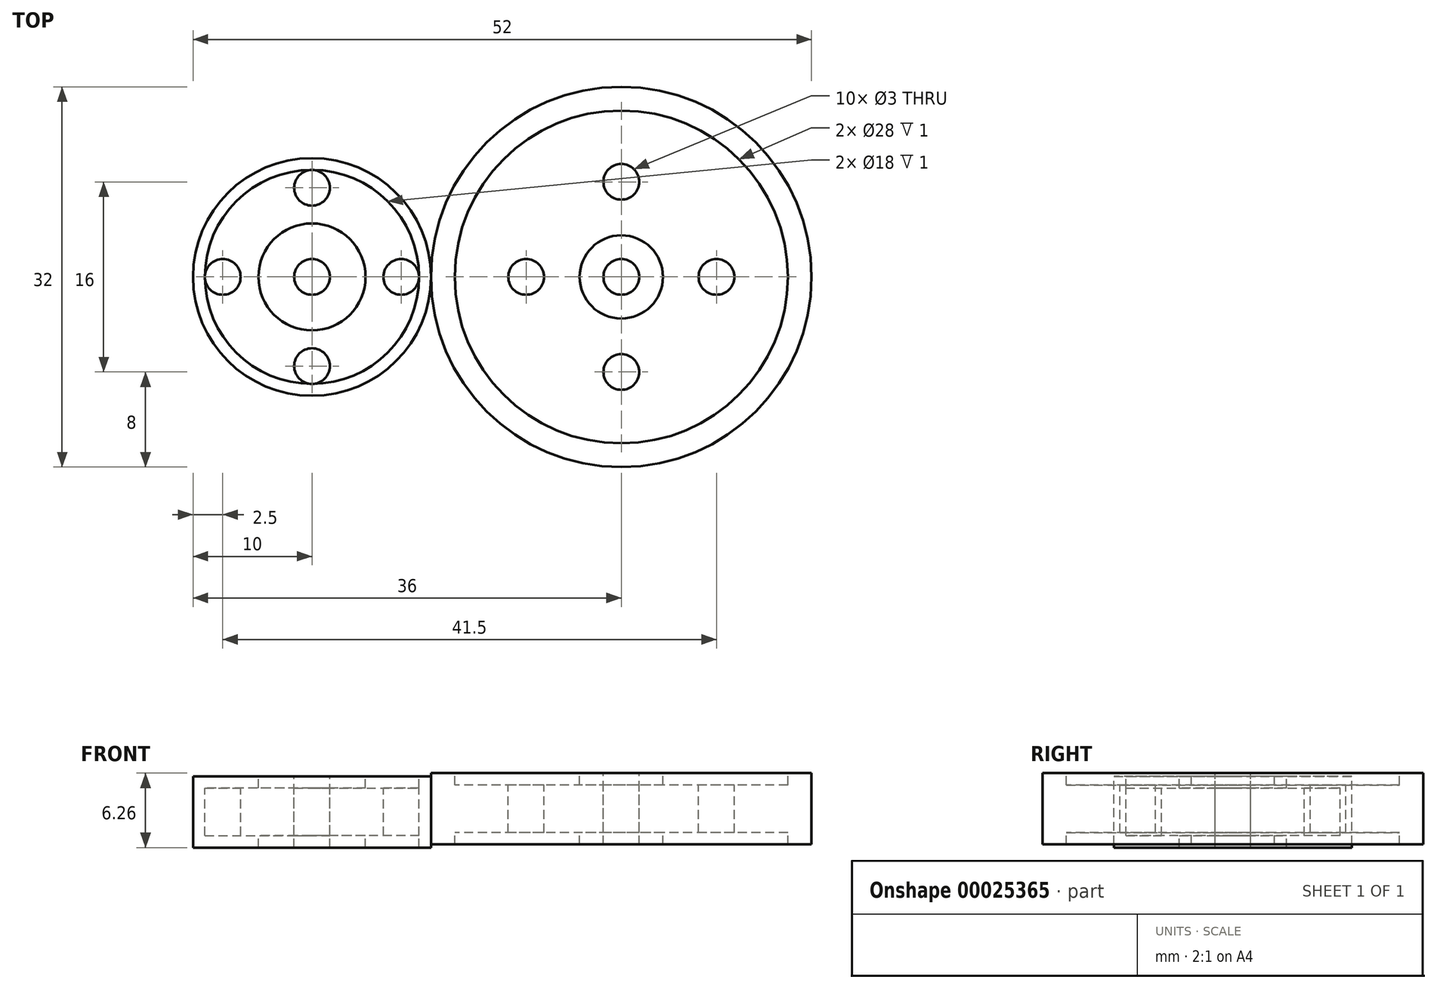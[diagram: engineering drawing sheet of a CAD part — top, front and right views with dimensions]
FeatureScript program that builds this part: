
annotation { "Feature Type Name" : "Feature", "Feature Type Description" : "" }
export const myFeature = defineFeature(function(context is Context, id is Id, definition is map)
    precondition{}
    {
        {
            var Q0;
            Q0=qCreatedBy(makeId("Front.planeOp"),FACE);
            var sketch = newSketch(context, id + "F0", { "sketchPlane" : qUnion([Q0])});
            skLineSegment(sketch, "E0", {"start": v(0, 6.2) * mm, "end": v(0, -6.7) * mm, "construction": true});
            skLineSegment(sketch, "E1.bottom", {"start": v(-4.5, 3.42) * mm, "end": v(-1.5, 3.42) * mm});
            skLineSegment(sketch, "E1.top", {"start": v(-4.5, -2.58) * mm, "end": v(-1.5, -2.58) * mm});
            skLineSegment(sketch, "E1.left", {"start": v(-4.5, 3.42) * mm, "end": v(-4.5, 2.42) * mm});
            skLineSegment(sketch, "E1.right", {"start": v(-1.5, 3.42) * mm, "end": v(-1.5, -2.58) * mm});
            skLineSegment(sketch, "E2.bottom", {"start": v(-4.5, 2.42) * mm, "end": v(-9, 2.42) * mm});
            skLineSegment(sketch, "E2.top", {"start": v(-4.5, -1.58) * mm, "end": v(-9, -1.58) * mm});
            skLineSegment(sketch, "E3.bottom", {"start": v(-9, 3.42) * mm, "end": v(-10, 3.42) * mm});
            skLineSegment(sketch, "E3.top", {"start": v(-9, -2.58) * mm, "end": v(-10, -2.58) * mm});
            skLineSegment(sketch, "E3.left", {"start": v(-9, 3.42) * mm, "end": v(-9, 2.42) * mm});
            skLineSegment(sketch, "E3.right", {"start": v(-10, 3.42) * mm, "end": v(-10, -2.58) * mm});
            skLineSegment(sketch, "E4.trimOffspring", {"start": v(-9, -1.58) * mm, "end": v(-9, -2.58) * mm});
            skLineSegment(sketch, "E5.trimOffspring", {"start": v(-4.5, -1.58) * mm, "end": v(-4.5, -2.58) * mm});
            skLineSegment(sketch, "E6", {"start": v(0, 6.2) * mm, "end": v(10, 6.2) * mm});
            skLineSegment(sketch, "E7", {"start": v(10, 6.2) * mm, "end": v(10, -16.38) * mm});
            skSolve(sketch);
        }
        {
            var Q0;
            Q0 = qSketchRegion(id + "F0", true);
            var Q1;
            Q1=sQuery(id+"F0.wireOp",EDGE,"E0");
            revolve(context, id + "F1", {"entities" : qUnion([Q0]), "axis" : qUnion([Q1]), "revolveType" : RevolveType.FULL});
        }
        {
            var Q0;
            Q0=makeQuery(id+"F1.opRevolve","SWEPT_FACE",FACE,{"disambiguationData":[OSD([sQuery(id+"F0.wireOp",EDGE,"E2.bottom")])]});
            var sketch = newSketch(context, id + "F2", { "sketchPlane" : qUnion([Q0])});
            skCircle(sketch, "E8", {"center": v(0, 7.5) * mm, "radius": 1.5 * mm});
            skCircle(sketch, "E9", {"center": v(7.5, 0) * mm, "radius": 1.5 * mm});
            skCircle(sketch, "E10", {"center": v(0, -7.5) * mm, "radius": 1.5 * mm});
            skCircle(sketch, "E11", {"center": v(-7.5, 0) * mm, "radius": 1.5 * mm});
            skSolve(sketch);
        }
        {
            var Q0;
            Q0=makeQuery(id+"F2.imprint","IMPRINT",FACE,{"disambiguationData":[TD([[makeQuery(id+"F2.imprint","IMPRINT",EDGE,{"derivedFrom":sQuery(id+"F2.wireOp",EDGE,"E9")}),1.0]])]});
            var Q1;
            Q1=makeQuery(id+"F2.imprint","IMPRINT",FACE,{"disambiguationData":[TD([[makeQuery(id+"F2.imprint","IMPRINT",EDGE,{"derivedFrom":sQuery(id+"F2.wireOp",EDGE,"E10")}),1.0]])]});
            var Q2;
            Q2=makeQuery(id+"F2.imprint","IMPRINT",FACE,{"disambiguationData":[TD([[makeQuery(id+"F2.imprint","IMPRINT",EDGE,{"derivedFrom":sQuery(id+"F2.wireOp",EDGE,"E11")}),1.0]])]});
            var Q3;
            Q3=makeQuery(id+"F2.imprint","IMPRINT",FACE,{"disambiguationData":[TD([[makeQuery(id+"F2.imprint","IMPRINT",EDGE,{"derivedFrom":sQuery(id+"F2.wireOp",EDGE,"E11")}),1.0]])]});
            var Q4;
            Q4=makeQuery(id+"F2.imprint","IMPRINT",FACE,{"disambiguationData":[TD([[makeQuery(id+"F2.imprint","IMPRINT",EDGE,{"derivedFrom":sQuery(id+"F2.wireOp",EDGE,"E8")}),1.0]])]});
            extrude(context, id + "F3", {"entities" : qUnion([Q0, Q1, Q2, Q3, Q4]), "operationType" : NewBodyOperationType.REMOVE, "oppositeDirection" : true, "depth" : 25 * mm});
        }
        {
            var Q0;
            Q0=qCreatedBy(makeId("Front.planeOp"),FACE);
            var sketch = newSketch(context, id + "F4", { "sketchPlane" : qUnion([Q0])});
            skLineSegment(sketch, "E12", {"start": v(26, 20.3) * mm, "end": v(26, 16.2) * mm, "construction": true});
            skLineSegment(sketch, "E13.bottom", {"start": v(22.5, 3.68) * mm, "end": v(24.5, 3.68) * mm});
            skLineSegment(sketch, "E13.top", {"start": v(22.5, -2.32) * mm, "end": v(24.5, -2.32) * mm});
            skLineSegment(sketch, "E13.left", {"start": v(22.5, 3.68) * mm, "end": v(22.5, 2.68) * mm});
            skLineSegment(sketch, "E13.right", {"start": v(24.5, 3.68) * mm, "end": v(24.5, -2.32) * mm});
            skLineSegment(sketch, "E14.bottom", {"start": v(22.5, 2.68) * mm, "end": v(12, 2.68) * mm});
            skLineSegment(sketch, "E14.top", {"start": v(22.5, -1.32) * mm, "end": v(12, -1.32) * mm});
            skLineSegment(sketch, "E15.bottom", {"start": v(12, 3.68) * mm, "end": v(10, 3.68) * mm});
            skLineSegment(sketch, "E15.top", {"start": v(12, -2.32) * mm, "end": v(10, -2.32) * mm});
            skLineSegment(sketch, "E15.left", {"start": v(12, 3.68) * mm, "end": v(12, 2.68) * mm});
            skLineSegment(sketch, "E15.right", {"start": v(10, 3.68) * mm, "end": v(10, -2.32) * mm});
            skLineSegment(sketch, "E16.trimOffspring", {"start": v(12, -1.32) * mm, "end": v(12, -2.32) * mm});
            skLineSegment(sketch, "E17.trimOffspring", {"start": v(22.5, -1.32) * mm, "end": v(22.5, -2.32) * mm});
            skLineSegment(sketch, "E18", {"start": v(10, 6.14) * mm, "end": v(10, -13.84) * mm});
            skSolve(sketch);
        }
        {
            var Q0;
            Q0 = qSketchRegion(id + "F4", true);
            var Q1;
            Q1=sQuery(id+"F4.wireOp",EDGE,"E12");
            revolve(context, id + "F5", {"entities" : qUnion([Q0]), "axis" : qUnion([Q1]), "revolveType" : RevolveType.FULL});
        }
        {
            var Q0;
            Q0=makeQuery(id+"F5.opRevolve","SWEPT_FACE",FACE,{"disambiguationData":[OSD([sQuery(id+"F4.wireOp",EDGE,"E14.bottom")])]});
            var sketch = newSketch(context, id + "F6", { "sketchPlane" : qUnion([Q0])});
            skCircle(sketch, "E19", {"center": v(26, 8) * mm, "radius": 1.5 * mm});
            skCircle(sketch, "E20", {"center": v(18, 0) * mm, "radius": 1.5 * mm});
            skCircle(sketch, "E21", {"center": v(34, 0) * mm, "radius": 1.5 * mm});
            skCircle(sketch, "E22", {"center": v(26, -8) * mm, "radius": 1.5 * mm});
            skPoint(sketch, "E23", {"position": v(26, 0) * mm});
            skSolve(sketch);
        }
        {
            var Q0;
            Q0 = qSketchRegion(id + "F6", true);
            extrude(context, id + "F7", {"entities" : qUnion([Q0]), "operationType" : NewBodyOperationType.REMOVE, "oppositeDirection" : true, "depth" : 25 * mm});
        }
    });
